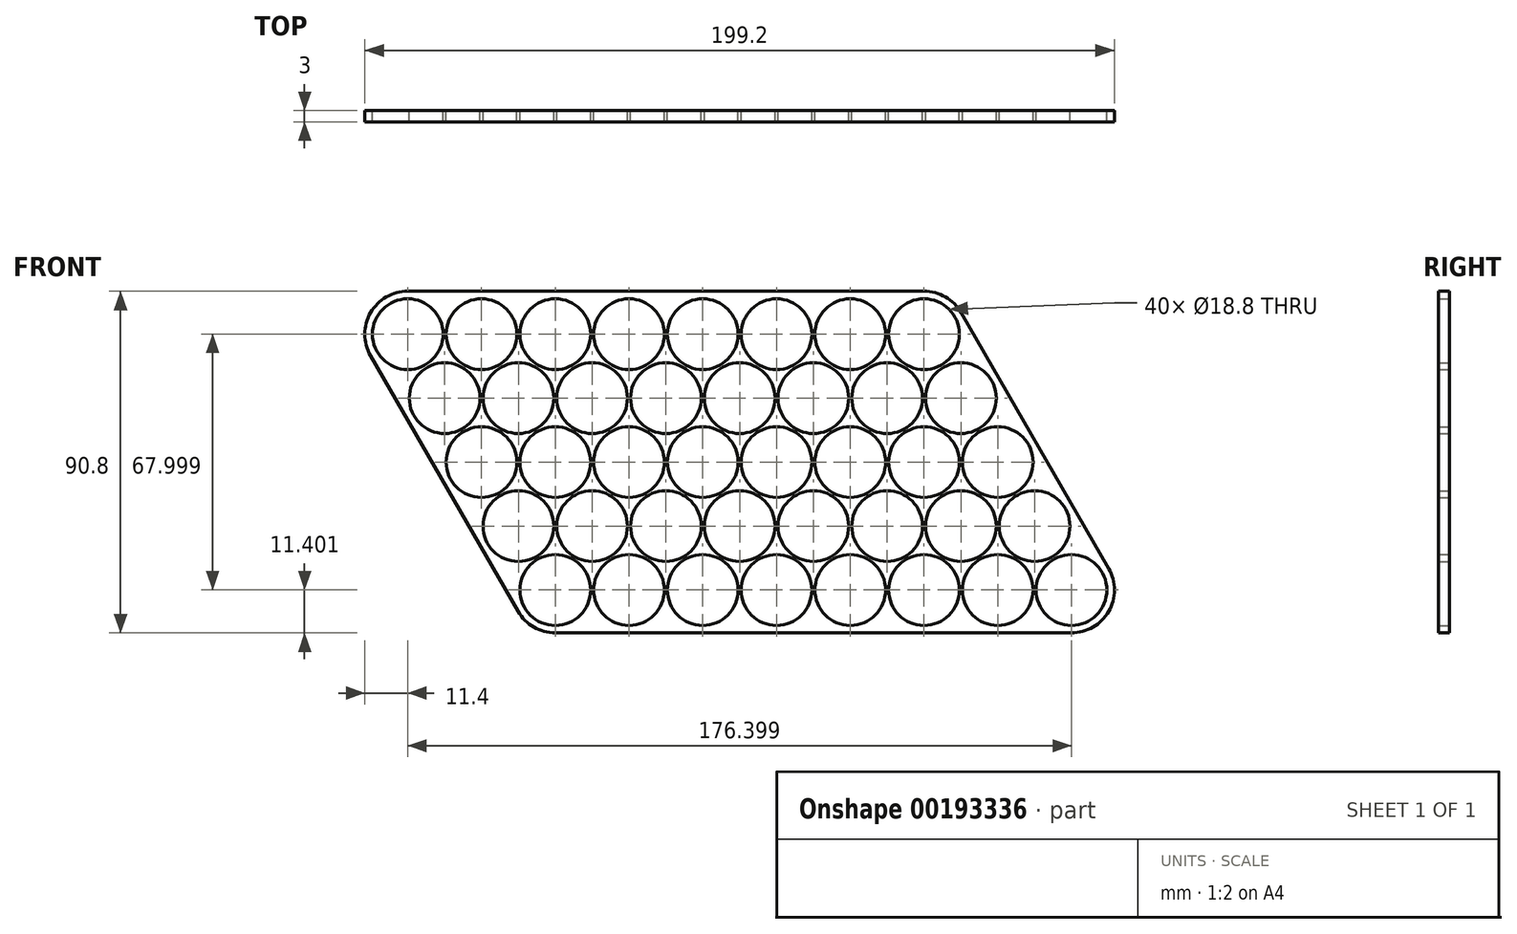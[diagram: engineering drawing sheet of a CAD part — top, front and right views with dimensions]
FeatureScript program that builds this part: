
annotation { "Feature Type Name" : "Feature", "Feature Type Description" : "" }
export const myFeature = defineFeature(function(context is Context, id is Id, definition is map)
    precondition{}
    {
        {
            var Q0;
            Q0=qCreatedBy(makeId("Front.planeOp"),FACE);
            var sketch = newSketch(context, id + "F0", { "sketchPlane" : qUnion([Q0])});
            skCircle(sketch, "E0", {"center": v(0, 0) * mm, "radius": 9.4 * mm});
            skCircle(sketch, "E1.1.0.0", {"center": v(19.6, 0) * mm, "radius": 9.4 * mm});
            skCircle(sketch, "E1.2.0.0", {"center": v(39.2, 0) * mm, "radius": 9.4 * mm});
            skCircle(sketch, "E1.3.0.0", {"center": v(58.8, 0) * mm, "radius": 9.4 * mm});
            skLineSegment(sketch, "E1.direction1", {"start": v(0, 0) * mm, "end": v(19.6, 0) * mm, "construction": true});
            skLineSegment(sketch, "E2", {"start": v(0, -17) * mm, "end": v(73.2, -17) * mm, "construction": true});
            skLineSegment(sketch, "E3", {"start": v(9.8, 0) * mm, "end": v(9.8, -17) * mm, "construction": true});
            skCircle(sketch, "E4", {"center": v(9.8, -17) * mm, "radius": 9.4 * mm});
            skCircle(sketch, "E5.1.0.0", {"center": v(29.4, -17) * mm, "radius": 9.4 * mm});
            skCircle(sketch, "E5.2.0.0", {"center": v(49, -17) * mm, "radius": 9.4 * mm});
            skCircle(sketch, "E5.3.0.0", {"center": v(68.6, -17) * mm, "radius": 9.4 * mm});
            skLineSegment(sketch, "E5.direction1", {"start": v(9.8, -17) * mm, "end": v(29.4, -17) * mm, "construction": true});
            skLineSegment(sketch, "E6", {"start": v(-8.14, -4.7) * mm, "end": v(1.66, -21.7) * mm});
            skLineSegment(sketch, "E7", {"start": v(0, 9.4) * mm, "end": v(58.8, 9.4) * mm});
            skLineSegment(sketch, "E8", {"start": v(9.8, -17) * mm, "end": v(9.8, -26.4) * mm, "construction": true});
            skLineSegment(sketch, "E9", {"start": v(68.6, -17) * mm, "end": v(68.6, -26.4) * mm, "construction": true});
            skArc(sketch, "E10", {"start": v(58.8, 9.4) * mm, "mid": v(63.5, 8.14) * mm, "end": v(66.94, 4.7) * mm});
            skArc(sketch, "E11", {"start": v(76.74, -12.3) * mm, "mid": v(76.74, -21.7) * mm, "end": v(68.6, -26.4) * mm});
            skArc(sketch, "E12", {"start": v(9.8, -26.4) * mm, "mid": v(5.1, -25.14) * mm, "end": v(1.66, -21.7) * mm});
            skArc(sketch, "E13", {"start": v(-8.14, -4.7) * mm, "mid": v(-8.14, 4.7) * mm, "end": v(0, 9.4) * mm});
            skArc(sketch, "E14.0", {"start": v(0, 11.4) * mm, "mid": v(-9.87, 5.7) * mm, "end": v(-9.88, -5.7) * mm});
            skLineSegment(sketch, "E15.0", {"start": v(0, 11.4) * mm, "end": v(58.8, 11.4) * mm});
            skLineSegment(sketch, "E16.0", {"start": v(-9.88, -5.7) * mm, "end": v(-0.08, -22.7) * mm});
            skArc(sketch, "E17.trimOffspring", {"start": v(9.8, -5.82) * mm, "mid": v(9.87, -5.71) * mm, "end": v(9.93, -5.6) * mm});
            skArc(sketch, "E18.trimOffspring", {"start": v(9.93, -5.6) * mm, "mid": v(9.86, -5.6) * mm, "end": v(9.8, -5.6) * mm});
            skCircle(sketch, "E19.0.4.0", {"center": v(78.4, 0) * mm, "radius": 9.4 * mm});
            skCircle(sketch, "E19.0.5.0", {"center": v(98, 0) * mm, "radius": 9.4 * mm});
            skCircle(sketch, "E20.0.4.0", {"center": v(88.2, -17) * mm, "radius": 9.4 * mm});
            skCircle(sketch, "E20.0.5.0", {"center": v(107.8, -17) * mm, "radius": 9.4 * mm});
            skLineSegment(sketch, "E21", {"start": v(58.8, 11.4) * mm, "end": v(98, 11.4) * mm});
            skLineSegment(sketch, "E22", {"start": v(0, 0) * mm, "end": v(9.8, -17) * mm, "construction": true});
            skCircle(sketch, "E23.1.0.0", {"center": v(19.6, -34) * mm, "radius": 9.4 * mm});
            skCircle(sketch, "E23.2.0.0", {"center": v(29.4, -51) * mm, "radius": 9.4 * mm});
            skLineSegment(sketch, "E23.direction1", {"start": v(9.8, -17) * mm, "end": v(19.6, -34) * mm, "construction": true});
            skCircle(sketch, "E24.1.0.0", {"center": v(39.2, -34) * mm, "radius": 9.4 * mm});
            skCircle(sketch, "E24.1.0.1", {"center": v(49, -51) * mm, "radius": 9.4 * mm});
            skCircle(sketch, "E24.2.0.0", {"center": v(58.8, -34) * mm, "radius": 9.4 * mm});
            skCircle(sketch, "E24.2.0.1", {"center": v(68.6, -51) * mm, "radius": 9.4 * mm});
            skCircle(sketch, "E24.3.0.0", {"center": v(78.4, -34) * mm, "radius": 9.4 * mm});
            skCircle(sketch, "E24.3.0.1", {"center": v(88.2, -51) * mm, "radius": 9.4 * mm});
            skCircle(sketch, "E24.4.0.0", {"center": v(98, -34) * mm, "radius": 9.4 * mm});
            skCircle(sketch, "E24.4.0.1", {"center": v(107.8, -51) * mm, "radius": 9.4 * mm});
            skCircle(sketch, "E24.5.0.0", {"center": v(117.6, -34) * mm, "radius": 9.4 * mm});
            skCircle(sketch, "E24.5.0.1", {"center": v(127.4, -51) * mm, "radius": 9.4 * mm});
            skLineSegment(sketch, "E24.direction1", {"start": v(19.6, -34) * mm, "end": v(39.2, -34) * mm, "construction": true});
            skLineSegment(sketch, "E25", {"start": v(-0.08, -22.7) * mm, "end": v(19.52, -56.7) * mm});
            skArc(sketch, "E26.0", {"start": v(29.27, -62.4) * mm, "mid": v(29.33, -62.4) * mm, "end": v(29.4, -62.4) * mm});
            skCircle(sketch, "E27.0.6.0", {"center": v(117.6, 0) * mm, "radius": 9.4 * mm});
            skCircle(sketch, "E27.0.7.0", {"center": v(137.2, 0) * mm, "radius": 9.4 * mm});
            skCircle(sketch, "E28.0.6.0", {"center": v(127.4, -17) * mm, "radius": 9.4 * mm});
            skCircle(sketch, "E28.0.7.0", {"center": v(147, -17) * mm, "radius": 9.4 * mm});
            skCircle(sketch, "E29.0.6.0", {"center": v(137.2, -34) * mm, "radius": 9.4 * mm});
            skCircle(sketch, "E29.2.6.0", {"center": v(147, -51) * mm, "radius": 9.4 * mm});
            skCircle(sketch, "E29.0.7.0", {"center": v(156.8, -34) * mm, "radius": 9.4 * mm});
            skCircle(sketch, "E29.2.7.0", {"center": v(166.6, -51) * mm, "radius": 9.4 * mm});
            skArc(sketch, "E30.0", {"start": v(147.08, 5.7) * mm, "mid": v(142.9, 9.87) * mm, "end": v(137.2, 11.4) * mm});
            skLineSegment(sketch, "E31", {"start": v(98, 11.4) * mm, "end": v(137.2, 11.4) * mm});
            skLineSegment(sketch, "E32", {"start": v(147.08, 5.7) * mm, "end": v(176.48, -45.3) * mm});
            skCircle(sketch, "E33.0.3.0", {"center": v(39.2, -68) * mm, "radius": 9.4 * mm});
            skCircle(sketch, "E34.1.0.0", {"center": v(58.8, -68) * mm, "radius": 9.4 * mm});
            skCircle(sketch, "E34.2.0.0", {"center": v(78.4, -68) * mm, "radius": 9.4 * mm});
            skCircle(sketch, "E34.3.0.0", {"center": v(98, -68) * mm, "radius": 9.4 * mm});
            skCircle(sketch, "E34.4.0.0", {"center": v(117.6, -68) * mm, "radius": 9.4 * mm});
            skCircle(sketch, "E34.5.0.0", {"center": v(137.2, -68) * mm, "radius": 9.4 * mm});
            skCircle(sketch, "E34.6.0.0", {"center": v(156.8, -68) * mm, "radius": 9.4 * mm});
            skCircle(sketch, "E34.7.0.0", {"center": v(176.4, -68) * mm, "radius": 9.4 * mm});
            skLineSegment(sketch, "E34.direction1", {"start": v(39.2, -68) * mm, "end": v(58.8, -68) * mm, "construction": true});
            skArc(sketch, "E35.0", {"start": v(29.32, -73.7) * mm, "mid": v(33.5, -77.87) * mm, "end": v(39.2, -79.4) * mm});
            skArc(sketch, "E36.0", {"start": v(176.4, -79.4) * mm, "mid": v(186.27, -73.7) * mm, "end": v(186.28, -62.3) * mm});
            skLineSegment(sketch, "E37", {"start": v(19.52, -56.7) * mm, "end": v(29.32, -73.7) * mm});
            skLineSegment(sketch, "E38", {"start": v(176.48, -45.3) * mm, "end": v(186.28, -62.3) * mm});
            skLineSegment(sketch, "E39", {"start": v(39.2, -79.4) * mm, "end": v(176.4, -79.4) * mm});
            skSolve(sketch);
        }
        {
            var Q0;
            Q0=qSketchRegion(id+"F0",true);
            var Q1;
            {var subQ3=sQuery(id+"F0.wireOp",EDGE,"E1.1.0.0");Q1=makeQuery(id+"F0.imprint","IMPRINT",FACE,{"disambiguationData":[TD([[makeQuery(id+"F0.imprint","IMPRINT",EDGE,{"derivedFrom":subQ3}),-1.0]])]});}
            extrude(context, id + "F1", {"entities" : qUnion([Q0, Q1]), "depth" : 3 * mm});
        }
    });
